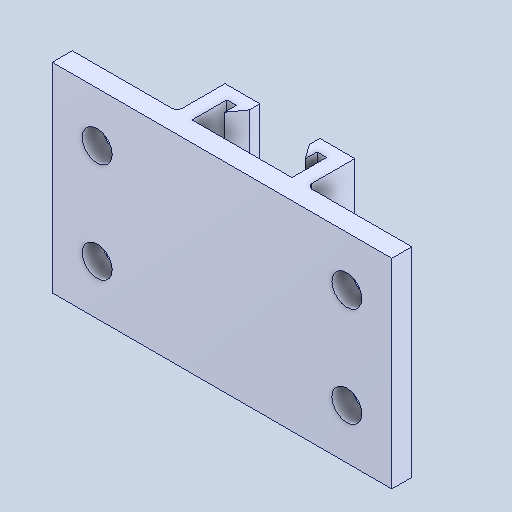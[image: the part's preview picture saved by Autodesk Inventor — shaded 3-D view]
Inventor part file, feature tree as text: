
AUTODESK INVENTOR PART (.ipt)
format: ipt  version: 2024.2 (Build 282272000, 272)  size: 116,224 bytes
history: native  units: in
note: dims shown in document units (in); Inventor stores cm internally (conversion verified against a paired STEP export)
features: fillet x1
ambient origin geometry x8: Origin, YZ Plane, XZ Plane, XY Plane, X Axis, Y Axis, Z Axis, Center Point
bodies: Solid1 (feature_tree)
feature tree (1):
  fillet  "Redondeo1"  [1 undecoded]
note: 1 required parameter value undecoded (feature->parameter linkage not recoverable at this tier; creation-order binding heuristic only, values carry confidence <= 0.55)
